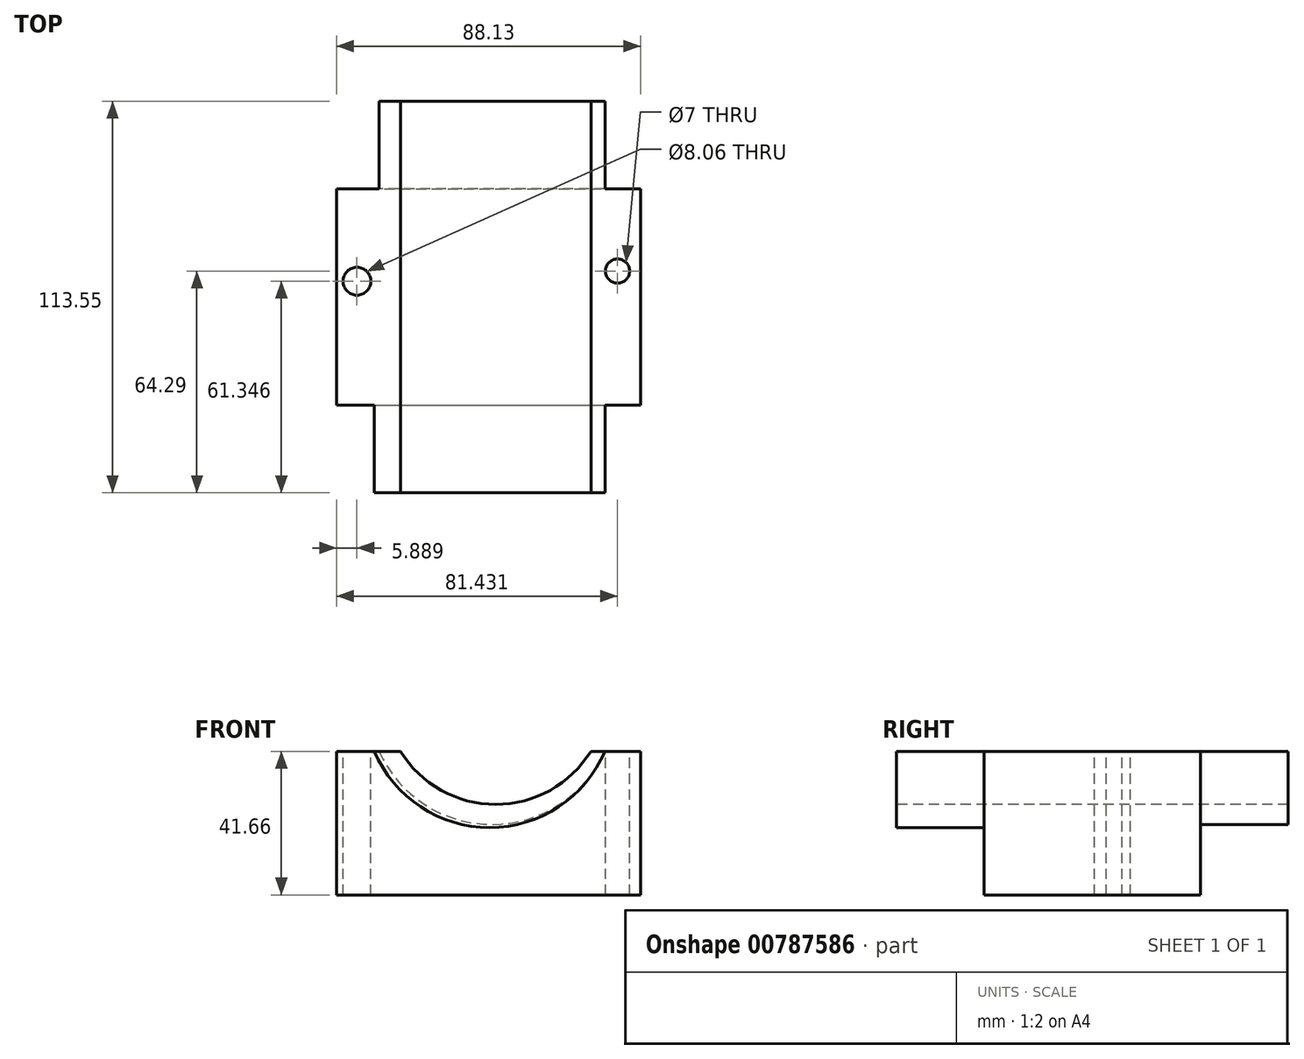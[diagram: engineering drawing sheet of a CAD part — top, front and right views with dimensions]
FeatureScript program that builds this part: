
annotation { "Feature Type Name" : "Feature", "Feature Type Description" : "" }
export const myFeature = defineFeature(function(context is Context, id is Id, definition is map)
    precondition{}
    {
        {
            var Q0;
            Q0=qCreatedBy(makeId("Top.planeOp"),FACE);
            var sketch = newSketch(context, id + "F0", { "sketchPlane" : qUnion([Q0])});
            skLineSegment(sketch, "E0.bottom", {"start": v(-39.7, 23.86) * mm, "end": v(48.43, 23.86) * mm});
            skLineSegment(sketch, "E0.top", {"start": v(-39.7, -38.89) * mm, "end": v(48.43, -38.89) * mm});
            skLineSegment(sketch, "E0.left", {"start": v(-39.7, 23.86) * mm, "end": v(-39.7, -38.89) * mm});
            skLineSegment(sketch, "E0.right", {"start": v(48.43, 23.86) * mm, "end": v(48.43, -38.89) * mm});
            skSolve(sketch);
        }
        {
            var Q0;
            Q0=makeQuery(id+"F0.imprint","IMPRINT",FACE,{"disambiguationData":[TD([[makeQuery(id+"F0.imprint","IMPRINT",EDGE,{"derivedFrom":sQuery(id+"F0.wireOp",EDGE,"E0.bottom")}),-1.0]])]});
            extrude(context, id + "F1", {"entities" : qUnion([Q0]), "depth" : 41.66 * mm, "offsetDistance" : 25.4 * mm});
        }
        {
            var Q0;
            Q0=makeQuery(id+"F1.opExtrude","SWEPT_FACE",FACE,{"disambiguationData":[OSD([sQuery(id+"F0.wireOp",EDGE,"E0.top")])]});
            var sketch = newSketch(context, id + "F2", { "sketchPlane" : qUnion([Q0])});
            skArc(sketch, "E1", {"start": v(-21.22, 41.66) * mm, "mid": v(6.4, 26.25) * mm, "end": v(34.01, 41.66) * mm});
            skArc(sketch, "E2", {"start": v(-28.73, 41.66) * mm, "mid": v(4.67, 19.53) * mm, "end": v(38.08, 41.66) * mm});
            skSolve(sketch);
        }
        {
            var Q0;
            {var subQ0=sQuery(id+"F2.wireOp",EDGE,"E1");Q0=makeQuery(id+"F2.imprint","IMPRINT",FACE,{"disambiguationData":[TD([[makeQuery(id+"F2.imprint","IMPRINT",EDGE,{"derivedFrom":subQ0}),1.0]])]});}
            extrude(context, id + "F3", {"entities" : qUnion([Q0]), "operationType" : NewBodyOperationType.REMOVE, "oppositeDirection" : true, "depth" : 2514.6 * mm, "offsetDistance" : 25.4 * mm});
        }
        {
            var Q0;
            {var subQ0=sQuery(id+"F2.wireOp",EDGE,"E1");Q0=makeQuery(id+"F2.imprint","IMPRINT",FACE,{"disambiguationData":[TD([[makeQuery(id+"F2.imprint","IMPRINT",EDGE,{"derivedFrom":subQ0}),-1.0]])]});}
            extrude(context, id + "F4", {"entities" : qUnion([Q0]), "operationType" : NewBodyOperationType.ADD, "depth" : 25.4 * mm, "offsetDistance" : 25.4 * mm});
        }
        {
            var Q0;
            Q0=makeQuery(id+"F1.opExtrude","SWEPT_FACE",FACE,{"disambiguationData":[OSD([sQuery(id+"F0.wireOp",EDGE,"E0.bottom")])]});
            var sketch = newSketch(context, id + "F5", { "sketchPlane" : qUnion([Q0])});
            skArc(sketch, "E3", {"start": v(-38.1, 41.66) * mm, "mid": v(-5.35, 20.44) * mm, "end": v(27.4, 41.66) * mm});
            skSolve(sketch);
        }
        {
            var Q0;
            {var subQ0=sQuery(id+"F5.wireOp",EDGE,"E3");Q0=makeQuery(id+"F5.imprint","IMPRINT",FACE,{"disambiguationData":[TD([[makeQuery(id+"F5.imprint","IMPRINT",EDGE,{"derivedFrom":subQ0}),1.0]])]});}
            extrude(context, id + "F6", {"entities" : qUnion([Q0]), "operationType" : NewBodyOperationType.ADD, "depth" : 25.4 * mm, "offsetDistance" : 25.4 * mm});
        }
        {
            var Q0;
            {var subQ0=sQuery(id+"F0.wireOp",EDGE,"E0.bottom");var subQ2=sQuery(id+"F0.wireOp",EDGE,"E0.left");var subQ3=sQuery(id+"F0.wireOp",EDGE,"E0.top");var subQ4=makeQuery(id+"F1.opExtrude","CAP_FACE",FACE,{"disambiguationData":[OSD([subQ0,subQ3,subQ2,sQuery(id+"F0.wireOp",EDGE,"E0.right")])],"isStart":false});var subQ5=makeQuery(id+"F1.opExtrude","SWEPT_FACE",FACE,{"disambiguationData":[OSD([subQ2])]});var subQ6=sQuery(id+"F2.wireOp",EDGE,"E1");var subQ8=makeQuery(id+"F3.boolean.opBoolean","SPLIT",EDGE,{"disambiguationData":[TD([subQ5])],"derivedFrom":makeQuery(id+"F1.opExtrude","CAP_EDGE",EDGE,{"disambiguationData":[OSD([subQ0])],"isStart":false})});var subQ9=makeQuery(id+"F1.opExtrude","CAP_EDGE",EDGE,{"disambiguationData":[OSD([subQ3])],"isStart":false});Q0=makeQuery(id+"F6.boolean.opBoolean","MERGE",FACE,{"derivedFrom":[makeQuery(id+"F4.boolean.opBoolean","MERGE",FACE,{"derivedFrom":[makeQuery(id+"F3.boolean.opBoolean","SPLIT",FACE,{"disambiguationData":[TD([subQ5])],"derivedFrom":subQ4}),makeQuery(id+"F4.opExtrude","SWEPT_FACE",FACE,{"disambiguationData":[OSD([subQ3]),TDD([makeQuery(id+"F2.imprint","IMPRINT",EDGE,{"disambiguationData":[TD([[makeQuery(id+"F2.imprint","INTERSECT",VERTEX,{"disambiguationData":[OD(0.0)],"derivedFrom":[subQ9,subQ6]}),1.0]])],"derivedFrom":subQ9})])]})]}),makeQuery(id+"F6.opExtrude","SWEPT_FACE",FACE,{"disambiguationData":[OSD([subQ0]),TDD([makeQuery(id+"F5.imprint","IMPRINT",EDGE,{"disambiguationData":[TD([[makeQuery(id+"F5.imprint","INTERSECT",VERTEX,{"derivedFrom":[subQ8,sQuery(id+"F5.wireOp",EDGE,"E3")]}),-1.0]])],"derivedFrom":subQ8})])]})]});}
            var sketch = newSketch(context, id + "F7", { "sketchPlane" : qUnion([Q0])});
            skCircle(sketch, "E4", {"center": v(-33.81, -2.94) * mm, "radius": 4.03 * mm});
            skSolve(sketch);
        }
        {
            var Q0;
            {var subQ0=sQuery(id+"F0.wireOp",EDGE,"E0.bottom");var subQ2=sQuery(id+"F0.wireOp",EDGE,"E0.right");var subQ3=makeQuery(id+"F1.opExtrude","SWEPT_FACE",FACE,{"disambiguationData":[OSD([subQ2])]});var subQ4=sQuery(id+"F0.wireOp",EDGE,"E0.top");var subQ5=makeQuery(id+"F1.opExtrude","CAP_FACE",FACE,{"disambiguationData":[OSD([subQ0,subQ4,sQuery(id+"F0.wireOp",EDGE,"E0.left"),subQ2])],"isStart":false});var subQ6=sQuery(id+"F2.wireOp",EDGE,"E1");var subQ8=makeQuery(id+"F3.boolean.opBoolean","SPLIT",EDGE,{"disambiguationData":[TD([subQ3])],"derivedFrom":makeQuery(id+"F1.opExtrude","CAP_EDGE",EDGE,{"disambiguationData":[OSD([subQ0])],"isStart":false})});var subQ9=makeQuery(id+"F1.opExtrude","CAP_EDGE",EDGE,{"disambiguationData":[OSD([subQ4])],"isStart":false});Q0=makeQuery(id+"F6.boolean.opBoolean","MERGE",FACE,{"derivedFrom":[makeQuery(id+"F4.boolean.opBoolean","MERGE",FACE,{"derivedFrom":[makeQuery(id+"F3.boolean.opBoolean","SPLIT",FACE,{"disambiguationData":[TD([subQ3])],"derivedFrom":subQ5}),makeQuery(id+"F4.opExtrude","SWEPT_FACE",FACE,{"disambiguationData":[OSD([subQ4]),TDD([makeQuery(id+"F2.imprint","IMPRINT",EDGE,{"disambiguationData":[TD([[makeQuery(id+"F2.imprint","INTERSECT",VERTEX,{"disambiguationData":[OD(1.0)],"derivedFrom":[subQ9,subQ6]}),-1.0]])],"derivedFrom":subQ9})])]})]}),makeQuery(id+"F6.opExtrude","SWEPT_FACE",FACE,{"disambiguationData":[OSD([subQ0]),TDD([makeQuery(id+"F5.imprint","IMPRINT",EDGE,{"disambiguationData":[TD([[makeQuery(id+"F5.imprint","INTERSECT",VERTEX,{"derivedFrom":[subQ8,sQuery(id+"F5.wireOp",EDGE,"E3")]}),1.0]])],"derivedFrom":subQ8})])]})]});}
            var sketch = newSketch(context, id + "F8", { "sketchPlane" : qUnion([Q0])});
            skCircle(sketch, "E5", {"center": v(41.73, 0) * mm, "radius": 3.5 * mm});
            skSolve(sketch);
        }
        {
            var Q0;
            Q0=makeQuery(id+"F7.imprint","IMPRINT",FACE,{"disambiguationData":[TD([[makeQuery(id+"F7.imprint","IMPRINT",EDGE,{"derivedFrom":sQuery(id+"F7.wireOp",EDGE,"E4")}),1.0]])]});
            var Q1;
            Q1=makeQuery(id+"F8.imprint","IMPRINT",FACE,{"disambiguationData":[TD([[makeQuery(id+"F8.imprint","IMPRINT",EDGE,{"derivedFrom":sQuery(id+"F8.wireOp",EDGE,"E5")}),1.0]])]});
            extrude(context, id + "F9", {"entities" : qUnion([Q0, Q1]), "operationType" : NewBodyOperationType.REMOVE, "oppositeDirection" : true, "depth" : 2514.6 * mm, "offsetDistance" : 25.4 * mm});
        }
    });
